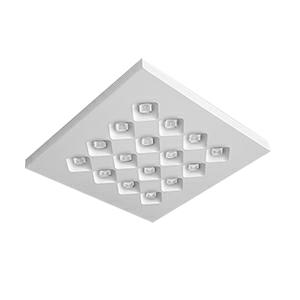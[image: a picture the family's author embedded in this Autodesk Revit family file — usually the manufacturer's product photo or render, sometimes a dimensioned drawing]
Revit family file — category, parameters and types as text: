
# Revit family: 3f_filippi_-_3f_diagon_3f_filippi_-_23032_a0686_-_3f_diagon_19w-840_ep_596x596___corn_plaf__9853
name_source: partatom
category: Lighting Fixtures
units: mm (PartAtom-declared; Revit-internal decimal feet)

## family parameters
Cut with Voids When Loaded = No
Host = Face
Light Source = No
Part Type = Normal
Room Calculation Point = No
Round Connector Dimension = Use Diameter
Shared = No

## types (1)
- 3F Filippi - 3F Dìagon (1 x LED, 3354 lm, 22 W, 4000 K)
    Apparent Load = 22 VA
    Approval mark = ENEC
    CIE Flux Codes = 67 96 100 100 100
    Color Rendering = 80
    Color Temperature = 4000 K
    Control Gear = Electronic ballast
    Default Elevation = 1800 mm
    Description = ILLUMINOTECHNICAL
Luminous efficiency 100% (DLOR 100%, ULOR 0%).
Initial luminous flux of the luminaire 3354 lm.
Emergency luminaire luminous flux BLF 26.4%.
Direct symmetric distribution.
Installation Interdistance Transv.D = 1.39 x hu - Long.D = 1.39 x hu.
Average luminance <1000 cd/m² for radial angles >65°.
Tabular UGR (CIE 117 - 4H-8H; S=0.25H; 70/50/20): RUG 16.5 - 16.5.
Beam angle: 93° - 92°.
Luminous efficacy 152 lm/W.
Lifetime (L95/B10): 30000 h. (tq+25°C)
Lifetime (L90/B10): 50000 h. (tq+25°C)
Lifetime (L80/B10): 80000 h. (tq+25°C)
Lifetime (L75/B10): 100000 h. (tq+25°C)
Sudden decreased luminous flux after 50000 hours: 0% (C0).
Photobiological safety in compliance with IEC/TR 62778: RG0 risk exempt, (IEC 62471).
In compliance with IEC/EN 62722-2-1 - IEC/EN 62717 standards.

SOURCE
Squared LED module 19W/840.
Energy efficiency class (UE 2019/2020 - UE 2019/2015): C.
CIE 13.3 Colour rendering index: CRI >80 (R9 <50%).
IES TM-30 Fidelity Index: Rf = 84 Rg = 95.
CCT nominal colour temperature 4000 K.
Colour initial tolerance (MacAdam): SDCM 3.

MECHANICAL
Housing in hot-galvanised steel, painted in white polyester.
Honeycombed diagonal screen in white anti-glare polycarbonate.
Rhomboidal lenses with differentiated surfaces, etched and prismatic to optimise the orientation of the luminous flux, in transparent methacrylate (PMMA).
Luminaire with limited surface temperature. - D - (EN 60598-2-24)
Dimensions: 600x600 mm, height 40 mm. Weight 7.02 kg.
IP43 protection degree for exposed part, IP20 for recessed part.
Mechanical strength to impacts IK06 (1 joule).
Glow-wire test resistance 650°C.

ELECTRICAL
Halogen Free electronic wiring 230V-50/60Hz, power factor 0.85, THD <25%, constant output current, class I, 1 driver.
Power of the luminaire 22 W.
CE - IEC 60598-1 - EN 60598-1.
EP maintained emergency wiring on board, 1h duration, 24h recharge; compliant with EN 60598-2-22, excluding high risk areas.
SAFE FLICKER: PstLM=<1 and SVM=<0.4 (IEC TR 61547-1 and IEC TR 63158), to ensure a more comfortable and safe light.
Ambient temperature from +5°C to +25°C.
Temperature class T6 max 85°C.
Quick connection.
Relative humidity UR: <85%.

INSTALLATION
Ceiling.
Height only 40 mm.
All accessories dedicated to this product are available on the Catalog and on our website www.3F-Filippi.com.

ACCESSORIES
A0686 - 596x596 Diagon frame for Ceiling installation.

APPLICATIONS
Environments: staterooms, with VDTs, offices.
Environments with exacting visual tasks, where diffused soft light for optimum visual comfort is required.

WARNING
Luminaire designed for disposal/recycling at end-of-life.
Replaceable (LED only) light source by a professional. Replaceable control gear by a professional.
    Height = 0 mm  [stored 0 ft]
    Lamp = 1 x LED
    Lamp Light Flux = 3354 lm
    Lamp Power = 22 W
    Lamp count = 1
    Length = 600 mm
    Lifetime = 50000 h
    Luminous efficacy = 152 lm/W
    Manufacturer = 3F Filippi
    ModVariant = No
    Model = 3F Filippi - 23032+A0686 - 3F Diagon 19W-840 EP 596x596 + Corn.plaf.
    Mounting Place = Ceiling
    Mounting Type = Recessed
    Number of Poles = 1
    OnlyDefault = Yes
    Power Factor = 1
    Product Name = 3F Filippi - 3F Dìagon
    Product group = recessed luminaire
    ProductGroupID = 4
    Protection Class = Protection class I
    Protection Degree = IP 20
    RLX_Detail_Level = 1
    RLX_Emergency_Light_Flux = 0 lm
    RLX_Emergency_Type = 0
    RLX_Emergency_Type_DB = No
    RlxData = <blob elided: 96037 chars, md5=b128719c>
    Socket = socket
    Standby Power = 0 W
    System Light Flux = 3354 lm
    System Power = 22 W
    Type Comments = Product without accessories
    Type Image = 3ffilippi_3f_diagon__a0686.jpg
    URL = http://relux.com
    VarID = ---
    Voltage = 0 V
    Weight = 0.00 kg
    Width = 600 mm

note: [stored X ft] marks values corroborated as IEEE doubles in the binary element streams (Revit-internal decimal feet)

## geometry (parser evidence)
native form markers: Blend x4, Sweep x9
no freeform markers — native parametric forms only
